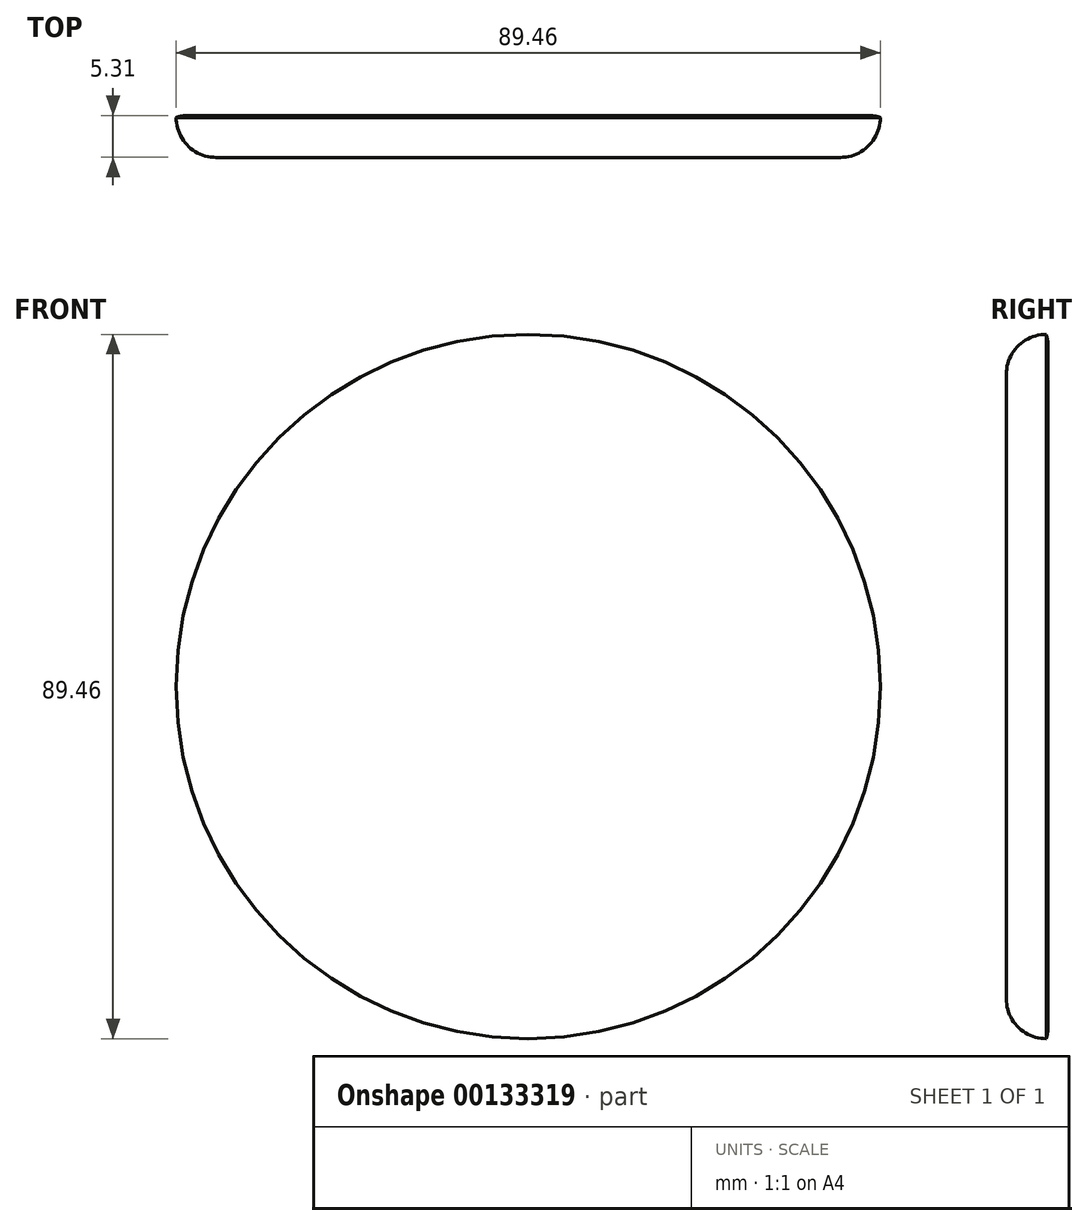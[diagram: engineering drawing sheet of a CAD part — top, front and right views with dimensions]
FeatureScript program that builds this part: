
annotation { "Feature Type Name" : "Feature", "Feature Type Description" : "" }
export const myFeature = defineFeature(function(context is Context, id is Id, definition is map)
    precondition{}
    {
        {
            var Q0;
            Q0=qCreatedBy(makeId("Front.planeOp"),FACE);
            var sketch = newSketch(context, id + "F0", { "sketchPlane" : qUnion([Q0])});
            skCircle(sketch, "E0", {"center": v(0, 0) * mm, "radius": 44.73 * mm});
            skSolve(sketch);
        }
        {
            var Q0;
            Q0 = qSketchRegion(id + "F0", true);
            extrude(context, id + "F1", {"entities" : qUnion([Q0]), "depth" : 5.3 * mm});
        }
        {
            var Q0;
            Q0=makeQuery(id+"F1.opExtrude","CAP_EDGE",EDGE,{"disambiguationData":[OSD([sQuery(id+"F0.wireOp",EDGE,"E0")])],"isStart":false});
            fillet(context, id + "F2", {"entities" : qUnion([Q0]), "radius" : 5.08 * mm, "tangentPropagation" : true, "allowEdgeOverflow" : false});
        }
        {
            var Q0;
            Q0=makeQuery(id+"F1.opExtrude","CAP_EDGE",EDGE,{"disambiguationData":[OSD([sQuery(id+"F0.wireOp",EDGE,"E0")])],"isStart":true});
            fillet(context, id + "F3", {"entities" : qUnion([Q0]), "radius" : 5.08 * mm, "tangentPropagation" : true, "allowEdgeOverflow" : false});
        }
    });
